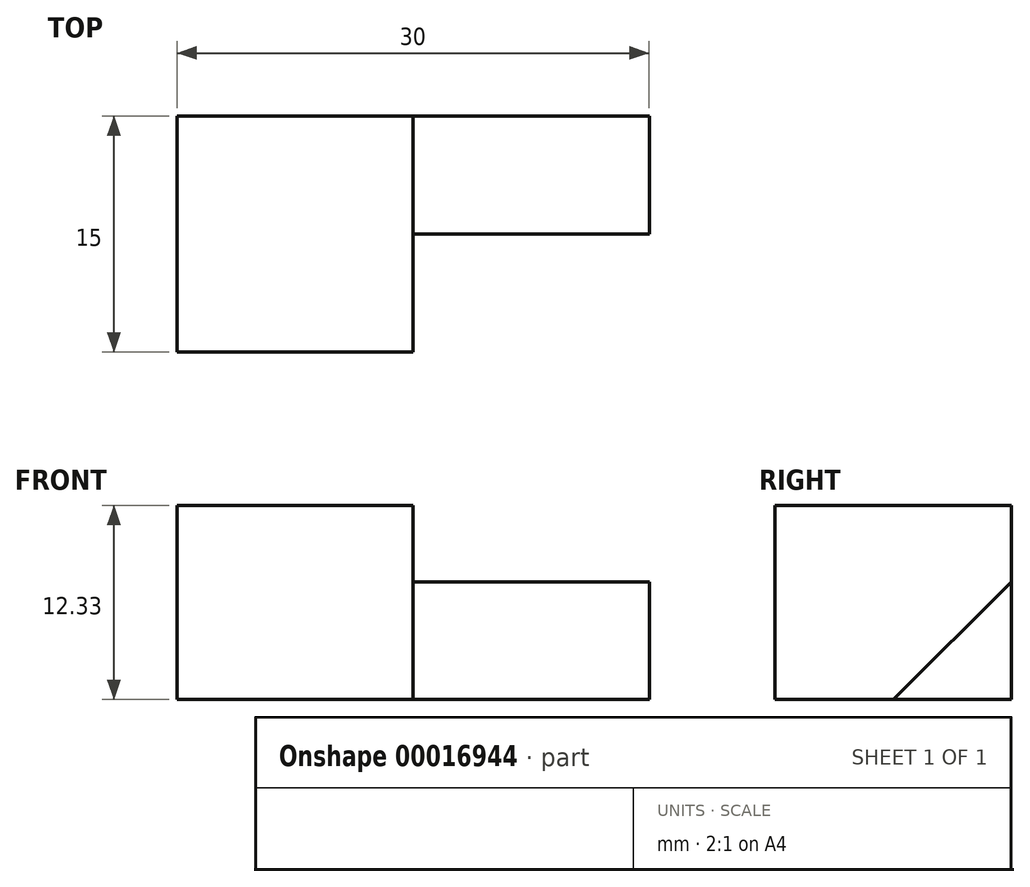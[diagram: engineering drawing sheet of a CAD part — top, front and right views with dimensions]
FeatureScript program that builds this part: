
annotation { "Feature Type Name" : "Feature", "Feature Type Description" : "" }
export const myFeature = defineFeature(function(context is Context, id is Id, definition is map)
    precondition{}
    {
        {
            var Q0;
            Q0=qCreatedBy(makeId("Front.planeOp"),FACE);
            var sketch = newSketch(context, id + "F0", { "sketchPlane" : qUnion([Q0])});
            skLineSegment(sketch, "E0", {"start": v(-6.2, 2.28) * mm, "end": v(-6.2, -10.05) * mm});
            skLineSegment(sketch, "E1", {"start": v(-6.2, -10.05) * mm, "end": v(8.8, -10.05) * mm});
            skLineSegment(sketch, "E2", {"start": v(8.8, -10.05) * mm, "end": v(8.8, 2.28) * mm});
            skLineSegment(sketch, "E3", {"start": v(-6.2, 2.28) * mm, "end": v(8.8, 2.28) * mm});
            skSolve(sketch);
        }
        {
            var Q0;
            Q0=makeQuery(id+"F0.imprint","IMPRINT",FACE,{"disambiguationData":[TD([[makeQuery(id+"F0.imprint","IMPRINT",EDGE,{"derivedFrom":sQuery(id+"F0.wireOp",EDGE,"E0")}),1.0]])]});
            extrude(context, id + "F1", {"entities" : qUnion([Q0]), "depth" : 15 * mm});
        }
        {
            var Q0;
            Q0=makeQuery(id+"F1.opExtrude","SWEPT_FACE",FACE,{"disambiguationData":[OSD([sQuery(id+"F0.wireOp",EDGE,"E2")])]});
            var sketch = newSketch(context, id + "F2", { "sketchPlane" : qUnion([Q0])});
            skLineSegment(sketch, "E4", {"start": v(0, -10.05) * mm, "end": v(-7.5, -10.05) * mm});
            skLineSegment(sketch, "E5", {"start": v(-7.5, -10.05) * mm, "end": v(0, -2.58) * mm});
            skLineSegment(sketch, "E6", {"start": v(0, -2.58) * mm, "end": v(0, -10.05) * mm});
            skSolve(sketch);
        }
        {
            var Q0;
            Q0=makeQuery(id+"F2.imprint","IMPRINT",FACE,{"disambiguationData":[TD([[makeQuery(id+"F2.imprint","IMPRINT",EDGE,{"derivedFrom":sQuery(id+"F2.wireOp",EDGE,"E4")}),1.0]])]});
            extrude(context, id + "F3", {"entities" : qUnion([Q0]), "operationType" : NewBodyOperationType.ADD, "depth" : 15 * mm});
        }
    });
